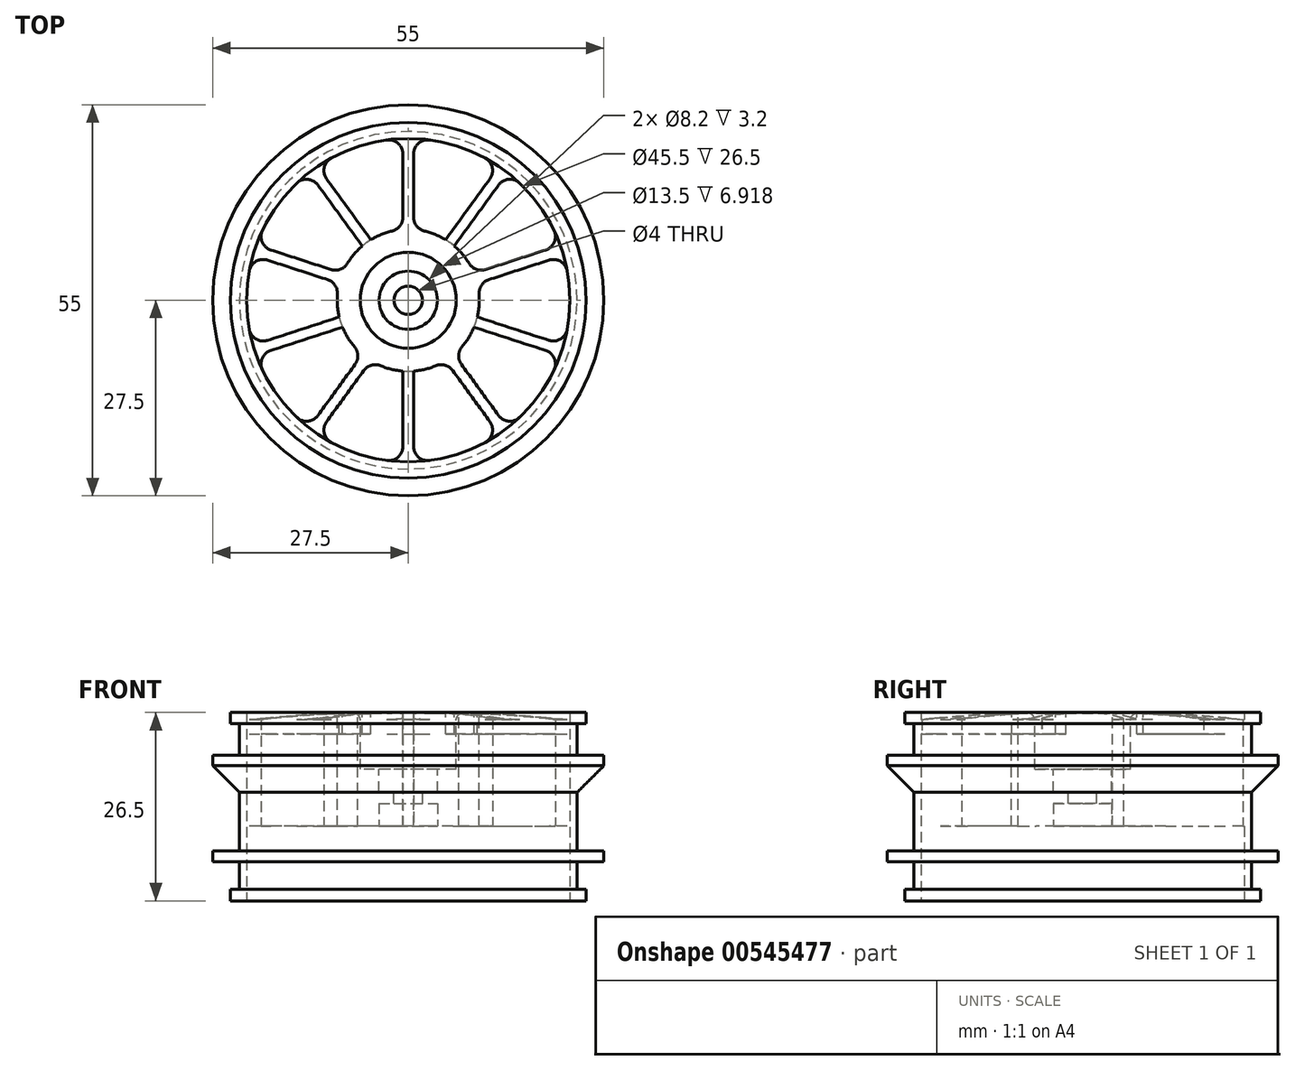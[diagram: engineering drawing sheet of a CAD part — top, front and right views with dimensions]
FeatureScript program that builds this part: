
annotation { "Feature Type Name" : "Feature", "Feature Type Description" : "" }
export const myFeature = defineFeature(function(context is Context, id is Id, definition is map)
    precondition{}
    {
        {
            var Q0;
            Q0=qCreatedBy(makeId("Top.planeOp"),FACE);
            var sketch = newSketch(context, id + "F0", { "sketchPlane" : qUnion([Q0])});
            skCircle(sketch, "E0", {"center": v(0, 0) * mm, "radius": 23.75 * mm});
            skCircle(sketch, "E1", {"center": v(0, 0) * mm, "radius": 22.75 * mm});
            skSolve(sketch);
        }
        {
            var Q0;
            Q0=qSketchRegion(id+"F0",true);
            extrude(context, id + "F1", {"entities" : qUnion([Q0]), "depth" : 26.5 * mm, "offsetDistance" : 25 * mm});
        }
        {
            var Q0;
            Q0=qCreatedBy(makeId("Top.planeOp"),FACE);
            var sketch = newSketch(context, id + "F2", { "sketchPlane" : qUnion([Q0])});
            skCircle(sketch, "E2", {"center": v(0, 0) * mm, "radius": 25 * mm});
            skCircle(sketch, "E3", {"center": v(0, 0) * mm, "radius": 22.75 * mm});
            skSolve(sketch);
        }
        {
            var Q0;
            Q0=qSketchRegion(id+"F2",true);
            extrude(context, id + "F3", {"entities" : qUnion([Q0]), "operationType" : NewBodyOperationType.ADD, "depth" : 1.6 * mm, "offsetDistance" : 25 * mm});
        }
        {
            var Q0;
            Q0=makeQuery(id+"F1.opExtrude","CAP_FACE",FACE,{"disambiguationData":[OSD([sQuery(id+"F0.wireOp",EDGE,"E0"),sQuery(id+"F0.wireOp",EDGE,"E1")])],"isStart":false});
            var sketch = newSketch(context, id + "F4", { "sketchPlane" : qUnion([Q0])});
            skCircle(sketch, "E4", {"center": v(0, 0) * mm, "radius": 22.75 * mm});
            skCircle(sketch, "E5", {"center": v(0, 0) * mm, "radius": 25 * mm});
            skSolve(sketch);
        }
        {
            var Q0;
            Q0=qSketchRegion(id+"F4",true);
            extrude(context, id + "F5", {"entities" : qUnion([Q0]), "operationType" : NewBodyOperationType.ADD, "oppositeDirection" : true, "depth" : 1.6 * mm, "offsetDistance" : 25 * mm});
        }
        {
            var Q0;
            Q0=qCreatedBy(makeId("Top.planeOp"),FACE);
            cPlane(context, id + "F6", {"entities" : qUnion([Q0]), "cplaneType" : CPlaneType.OFFSET, "offset" : 5.5 * mm, "width" : 150 * mm, "height" : 150 * mm});
        }
        {
            var Q0;
            Q0=qCreatedBy(id+"F6.planeOp",FACE);
            var sketch = newSketch(context, id + "F7", { "sketchPlane" : qUnion([Q0])});
            skCircle(sketch, "E6", {"center": v(0, 0) * mm, "radius": 27.5 * mm});
            skCircle(sketch, "E7", {"center": v(0, 0) * mm, "radius": 22.75 * mm});
            skSolve(sketch);
        }
        {
            var Q0;
            Q0=qSketchRegion(id+"F7",true);
            extrude(context, id + "F8", {"entities" : qUnion([Q0]), "operationType" : NewBodyOperationType.ADD, "depth" : 1.5 * mm, "offsetDistance" : 25 * mm});
        }
        {
            var Q0;
            Q0=qCreatedBy(makeId("Top.planeOp"),FACE);
            cPlane(context, id + "F9", {"entities" : qUnion([Q0]), "cplaneType" : CPlaneType.OFFSET, "offset" : 19 * mm, "width" : 150 * mm, "height" : 150 * mm});
        }
        {
            var Q0;
            Q0=qCreatedBy(id+"F9.planeOp",FACE);
            var sketch = newSketch(context, id + "F10", { "sketchPlane" : qUnion([Q0])});
            skCircle(sketch, "E8", {"center": v(0, 0) * mm, "radius": 27.5 * mm});
            skCircle(sketch, "E9", {"center": v(0, 0) * mm, "radius": 22.75 * mm});
            skSolve(sketch);
        }
        {
            var Q0;
            Q0=qSketchRegion(id+"F10",true);
            extrude(context, id + "F11", {"entities" : qUnion([Q0]), "operationType" : NewBodyOperationType.ADD, "depth" : 1.5 * mm, "offsetDistance" : 25 * mm});
        }
        {
            var Q0;
            Q0=makeQuery(id+"F5.boolean.opBoolean","MERGE",FACE,{"derivedFrom":[makeQuery(id+"F1.opExtrude","CAP_FACE",FACE,{"disambiguationData":[OSD([sQuery(id+"F0.wireOp",EDGE,"E0"),sQuery(id+"F0.wireOp",EDGE,"E1")])],"isStart":false}),makeQuery(id+"F5.opExtrude","CAP_FACE",FACE,{"disambiguationData":[OSD([sQuery(id+"F4.wireOp",EDGE,"E4"),sQuery(id+"F4.wireOp",EDGE,"E5")])],"isStart":true})]});
            var sketch = newSketch(context, id + "F12", { "sketchPlane" : qUnion([Q0])});
            skLineSegment(sketch, "E10.top", {"start": v(-0.75, 23) * mm, "end": v(0.75, 23) * mm});
            skLineSegment(sketch, "E10.left", {"start": v(-0.75, 9.97) * mm, "end": v(-0.75, 23) * mm});
            skLineSegment(sketch, "E10.right", {"start": v(0.75, 9.97) * mm, "end": v(0.75, 23) * mm});
            skArc(sketch, "E11", {"start": v(-0.75, 9.97) * mm, "mid": v(-5.88, 8.1) * mm, "end": v(-9.25, 3.8) * mm});
            skLineSegment(sketch, "E12.1.0", {"start": v(9.25, 3.8) * mm, "end": v(21.64, 7.82) * mm});
            skLineSegment(sketch, "E12.1.1", {"start": v(9.72, 2.37) * mm, "end": v(22.1, 6.4) * mm});
            skLineSegment(sketch, "E12.1.2", {"start": v(21.64, 7.82) * mm, "end": v(22.1, 6.4) * mm});
            skLineSegment(sketch, "E12.2.0", {"start": v(6.47, -7.63) * mm, "end": v(14.13, -18.17) * mm});
            skLineSegment(sketch, "E12.2.1", {"start": v(5.25, -8.5) * mm, "end": v(12.91, -19.05) * mm});
            skLineSegment(sketch, "E12.2.2", {"start": v(14.13, -18.17) * mm, "end": v(12.91, -19.05) * mm});
            skLineSegment(sketch, "E12.3.0", {"start": v(-5.25, -8.5) * mm, "end": v(-12.91, -19.05) * mm});
            skLineSegment(sketch, "E12.3.1", {"start": v(-6.47, -7.63) * mm, "end": v(-14.13, -18.17) * mm});
            skLineSegment(sketch, "E12.3.2", {"start": v(-12.91, -19.05) * mm, "end": v(-14.13, -18.17) * mm});
            skLineSegment(sketch, "E12.4.0", {"start": v(-9.72, 2.37) * mm, "end": v(-22.1, 6.4) * mm});
            skLineSegment(sketch, "E12.4.1", {"start": v(-9.25, 3.8) * mm, "end": v(-21.64, 7.82) * mm});
            skLineSegment(sketch, "E12.4.2", {"start": v(-22.1, 6.4) * mm, "end": v(-21.64, 7.82) * mm});
            skLineSegment(sketch, "E12.anchor1", {"start": v(0, 0) * mm, "end": v(-0.75, 9.97) * mm, "construction": true});
            skLineSegment(sketch, "E12.anchor2", {"start": v(0, 0) * mm, "end": v(-9.72, 2.37) * mm, "construction": true});
            skArc(sketch, "E13.trimOffspring", {"start": v(-9.72, 2.37) * mm, "mid": v(-9.51, -3.1) * mm, "end": v(-6.47, -7.63) * mm});
            skArc(sketch, "E14.trimOffspring", {"start": v(-5.25, -8.5) * mm, "mid": v(0, -10) * mm, "end": v(5.25, -8.5) * mm});
            skArc(sketch, "E15.trimOffspring", {"start": v(6.47, -7.63) * mm, "mid": v(9.51, -3.1) * mm, "end": v(9.72, 2.37) * mm});
            skArc(sketch, "E16.trimOffspring", {"start": v(9.25, 3.8) * mm, "mid": v(5.88, 8.1) * mm, "end": v(0.75, 9.97) * mm});
            skSolve(sketch);
        }
        {
            var Q0;
            Q0=qSketchRegion(id+"F12",true);
            extrude(context, id + "F13", {"entities" : qUnion([Q0]), "operationType" : NewBodyOperationType.ADD, "oppositeDirection" : true, "depth" : 16 * mm, "offsetDistance" : 25 * mm});
        }
        {
            var Q0;
            Q0=makeQuery(id+"F11.boolean.opBoolean","INTERSECT",EDGE,{"derivedFrom":[makeQuery(id+"F8.boolean.opBoolean","SPLIT",FACE,{"disambiguationData":[TD([makeQuery(id+"F5.opExtrude","CAP_FACE",FACE,{"disambiguationData":[OSD([sQuery(id+"F4.wireOp",EDGE,"E4"),sQuery(id+"F4.wireOp",EDGE,"E5")])],"isStart":false})])],"derivedFrom":makeQuery(id+"F1.opExtrude","SWEPT_FACE",FACE,{"disambiguationData":[OSD([sQuery(id+"F0.wireOp",EDGE,"E0")])]})}),makeQuery(id+"F11.opExtrude","CAP_FACE",FACE,{"disambiguationData":[OSD([sQuery(id+"F10.wireOp",EDGE,"E8"),sQuery(id+"F10.wireOp",EDGE,"E9")])],"isStart":true})]});
            chamfer(context, id + "F14", {"entities" : qUnion([Q0]), "width" : 3.75 * mm, "tangentPropagation" : true});
        }
        {
            var Q0;
            Q0=makeQuery(id+"F13.boolean.opBoolean","MERGE",FACE,{"derivedFrom":[makeQuery(id+"F5.boolean.opBoolean","MERGE",FACE,{"derivedFrom":[makeQuery(id+"F1.opExtrude","CAP_FACE",FACE,{"disambiguationData":[OSD([sQuery(id+"F0.wireOp",EDGE,"E0"),sQuery(id+"F0.wireOp",EDGE,"E1")])],"isStart":false}),makeQuery(id+"F5.opExtrude","CAP_FACE",FACE,{"disambiguationData":[OSD([sQuery(id+"F4.wireOp",EDGE,"E4"),sQuery(id+"F4.wireOp",EDGE,"E5")])],"isStart":true})]}),makeQuery(id+"F13.opExtrude","CAP_FACE",FACE,{"disambiguationData":[OSD([sQuery(id+"F12.wireOp",EDGE,"E10.top"),sQuery(id+"F12.wireOp",EDGE,"E10.left"),sQuery(id+"F12.wireOp",EDGE,"E10.right"),sQuery(id+"F12.wireOp",EDGE,"E11"),sQuery(id+"F12.wireOp",EDGE,"E12.1.0"),sQuery(id+"F12.wireOp",EDGE,"E12.1.1"),sQuery(id+"F12.wireOp",EDGE,"E12.1.2"),sQuery(id+"F12.wireOp",EDGE,"E12.2.0"),sQuery(id+"F12.wireOp",EDGE,"E12.2.1"),sQuery(id+"F12.wireOp",EDGE,"E12.2.2"),sQuery(id+"F12.wireOp",EDGE,"E12.3.0"),sQuery(id+"F12.wireOp",EDGE,"E12.3.1"),sQuery(id+"F12.wireOp",EDGE,"E12.3.2"),sQuery(id+"F12.wireOp",EDGE,"E12.4.0"),sQuery(id+"F12.wireOp",EDGE,"E12.4.1"),sQuery(id+"F12.wireOp",EDGE,"E12.4.2"),sQuery(id+"F12.wireOp",EDGE,"E13.trimOffspring"),sQuery(id+"F12.wireOp",EDGE,"E14.trimOffspring"),sQuery(id+"F12.wireOp",EDGE,"E15.trimOffspring"),sQuery(id+"F12.wireOp",EDGE,"E16.trimOffspring")])],"isStart":true})]});
            var sketch = newSketch(context, id + "F15", { "sketchPlane" : qUnion([Q0])});
            skArc(sketch, "E17", {"start": v(-0.75, 9.97) * mm, "mid": v(-3.1, 9.51) * mm, "end": v(-5.25, 8.5) * mm});
            skLineSegment(sketch, "E18", {"start": v(-0.75, 9.97) * mm, "end": v(-0.75, 22.97) * mm});
            skLineSegment(sketch, "E19", {"start": v(0.75, 22.97) * mm, "end": v(0.75, 9.97) * mm});
            skLineSegment(sketch, "E20.1.0", {"start": v(-6.47, 7.63) * mm, "end": v(-14.11, 18.14) * mm});
            skLineSegment(sketch, "E20.1.1", {"start": v(-12.9, 19.02) * mm, "end": v(-5.25, 8.5) * mm});
            skLineSegment(sketch, "E20.2.0", {"start": v(-9.72, 2.37) * mm, "end": v(-22.08, 6.38) * mm});
            skLineSegment(sketch, "E20.2.1", {"start": v(-21.62, 7.8) * mm, "end": v(-9.25, 3.8) * mm});
            skLineSegment(sketch, "E20.3.0", {"start": v(-9.25, -3.8) * mm, "end": v(-21.62, -7.81) * mm});
            skLineSegment(sketch, "E20.3.1", {"start": v(-22.08, -6.39) * mm, "end": v(-9.72, -2.37) * mm});
            skLineSegment(sketch, "E20.4.0", {"start": v(-5.25, -8.5) * mm, "end": v(-12.9, -19.03) * mm});
            skLineSegment(sketch, "E20.4.1", {"start": v(-14.1, -18.15) * mm, "end": v(-6.47, -7.63) * mm});
            skLineSegment(sketch, "E20.5.0", {"start": v(0.75, -9.97) * mm, "end": v(0.75, -22.97) * mm});
            skLineSegment(sketch, "E20.5.1", {"start": v(-0.75, -22.97) * mm, "end": v(-0.75, -9.97) * mm});
            skLineSegment(sketch, "E20.6.0", {"start": v(6.47, -7.63) * mm, "end": v(14.11, -18.14) * mm});
            skLineSegment(sketch, "E20.6.1", {"start": v(12.9, -19.02) * mm, "end": v(5.25, -8.5) * mm});
            skLineSegment(sketch, "E20.7.0", {"start": v(9.72, -2.37) * mm, "end": v(22.08, -6.38) * mm});
            skLineSegment(sketch, "E20.7.1", {"start": v(21.62, -7.8) * mm, "end": v(9.25, -3.8) * mm});
            skLineSegment(sketch, "E20.8.0", {"start": v(9.25, 3.8) * mm, "end": v(21.62, 7.81) * mm});
            skLineSegment(sketch, "E20.8.1", {"start": v(22.08, 6.39) * mm, "end": v(9.72, 2.37) * mm});
            skLineSegment(sketch, "E20.9.0", {"start": v(5.25, 8.5) * mm, "end": v(12.9, 19.03) * mm});
            skLineSegment(sketch, "E20.9.1", {"start": v(14.1, 18.15) * mm, "end": v(6.47, 7.63) * mm});
            skArc(sketch, "E21.trimOffspring", {"start": v(-9.72, 2.37) * mm, "mid": v(-10, 0) * mm, "end": v(-9.72, -2.37) * mm});
            skArc(sketch, "E22.trimOffspring", {"start": v(-5.25, -8.5) * mm, "mid": v(-3.1, -9.51) * mm, "end": v(-0.75, -9.97) * mm});
            skArc(sketch, "E23.trimOffspring", {"start": v(9.72, -2.37) * mm, "mid": v(10, 0) * mm, "end": v(9.72, 2.37) * mm});
            skArc(sketch, "E24.trimOffspring", {"start": v(6.47, -7.63) * mm, "mid": v(8.1, -5.88) * mm, "end": v(9.25, -3.8) * mm});
            skArc(sketch, "E25.trimOffspring", {"start": v(0.75, -9.97) * mm, "mid": v(3.1, -9.51) * mm, "end": v(5.25, -8.5) * mm});
            skArc(sketch, "E26.trimOffspring", {"start": v(-9.25, -3.8) * mm, "mid": v(-8.1, -5.88) * mm, "end": v(-6.47, -7.63) * mm});
            skArc(sketch, "E27.trimOffspring", {"start": v(-6.47, 7.63) * mm, "mid": v(-8.1, 5.88) * mm, "end": v(-9.25, 3.8) * mm});
            skArc(sketch, "E28.trimOffspring", {"start": v(5.25, 8.5) * mm, "mid": v(3.1, 9.51) * mm, "end": v(0.75, 9.97) * mm});
            skArc(sketch, "E29.trimOffspring", {"start": v(9.25, 3.8) * mm, "mid": v(8.1, 5.88) * mm, "end": v(6.47, 7.63) * mm});
            skLineSegment(sketch, "E30", {"start": v(-12.9, 19.02) * mm, "end": v(-14.11, 18.14) * mm});
            skLineSegment(sketch, "E31", {"start": v(-21.62, 7.8) * mm, "end": v(-22.08, 6.38) * mm});
            skLineSegment(sketch, "E32", {"start": v(-22.08, -6.39) * mm, "end": v(-21.62, -7.81) * mm});
            skLineSegment(sketch, "E33", {"start": v(-14.1, -18.15) * mm, "end": v(-12.9, -19.03) * mm});
            skLineSegment(sketch, "E34", {"start": v(-0.75, -22.97) * mm, "end": v(0.75, -22.97) * mm});
            skLineSegment(sketch, "E35", {"start": v(14.11, -18.14) * mm, "end": v(12.9, -19.02) * mm});
            skLineSegment(sketch, "E36", {"start": v(22.08, -6.38) * mm, "end": v(21.62, -7.8) * mm});
            skLineSegment(sketch, "E37", {"start": v(21.62, 7.81) * mm, "end": v(22.08, 6.39) * mm});
            skLineSegment(sketch, "E38", {"start": v(12.9, 19.03) * mm, "end": v(14.1, 18.15) * mm});
            skLineSegment(sketch, "E39", {"start": v(-0.75, 22.97) * mm, "end": v(0.75, 22.97) * mm});
            skSolve(sketch);
        }
        {
            var Q0;
            Q0=qSketchRegion(id+"F15",true);
            extrude(context, id + "F16", {"entities" : qUnion([Q0]), "operationType" : NewBodyOperationType.ADD, "oppositeDirection" : true, "depth" : 3 * mm, "offsetDistance" : 25 * mm});
        }
        {
            var Q0;
            Q0=makeQuery(id+"F16.boolean.opBoolean","INTERSECT",EDGE,{"derivedFrom":[makeQuery(id+"F1.opExtrude","SWEPT_FACE",FACE,{"disambiguationData":[OSD([sQuery(id+"F0.wireOp",EDGE,"E1")])]}),makeQuery(id+"F16.opExtrude","SWEPT_FACE",FACE,{"disambiguationData":[OSD([sQuery(id+"F15.wireOp",EDGE,"E20.1.0")])]})]});
            var Q1;
            Q1=makeQuery(id+"F16.boolean.opBoolean","INTERSECT",EDGE,{"derivedFrom":[makeQuery(id+"F1.opExtrude","SWEPT_FACE",FACE,{"disambiguationData":[OSD([sQuery(id+"F0.wireOp",EDGE,"E1")])]}),makeQuery(id+"F16.opExtrude","SWEPT_FACE",FACE,{"disambiguationData":[OSD([sQuery(id+"F15.wireOp",EDGE,"E20.1.1")])]})]});
            var Q2;
            Q2=makeQuery(id+"F16.opExtrude","SWEPT_EDGE",EDGE,{"disambiguationData":[OSD([sQuery(id+"F12.wireOp",EDGE,"E11"),sQuery(id+"F15.wireOp",EDGE,"E20.1.0"),sQuery(id+"F15.wireOp",EDGE,"E27.trimOffspring")])]});
            var Q3;
            Q3=makeQuery(id+"F13.boolean.opBoolean","INTERSECT",EDGE,{"derivedFrom":[makeQuery(id+"F1.opExtrude","SWEPT_FACE",FACE,{"disambiguationData":[OSD([sQuery(id+"F0.wireOp",EDGE,"E1")])]}),makeQuery(id+"F13.opExtrude","SWEPT_FACE",FACE,{"disambiguationData":[OSD([sQuery(id+"F12.wireOp",EDGE,"E12.4.1")])]})]});
            var Q4;
            Q4=makeQuery(id+"F13.opExtrude","SWEPT_EDGE",EDGE,{"disambiguationData":[OSD([sQuery(id+"F12.wireOp",EDGE,"E11"),sQuery(id+"F12.wireOp",EDGE,"E12.4.1")])]});
            var Q5;
            Q5=makeQuery(id+"F13.opExtrude","SWEPT_EDGE",EDGE,{"disambiguationData":[OSD([sQuery(id+"F12.wireOp",EDGE,"E10.left"),sQuery(id+"F12.wireOp",EDGE,"E11")])]});
            var Q6;
            Q6=makeQuery(id+"F13.boolean.opBoolean","INTERSECT",EDGE,{"derivedFrom":[makeQuery(id+"F1.opExtrude","SWEPT_FACE",FACE,{"disambiguationData":[OSD([sQuery(id+"F0.wireOp",EDGE,"E1")])]}),makeQuery(id+"F13.opExtrude","SWEPT_FACE",FACE,{"disambiguationData":[OSD([sQuery(id+"F12.wireOp",EDGE,"E10.left")])]})]});
            var Q7;
            Q7=makeQuery(id+"F16.opExtrude","SWEPT_EDGE",EDGE,{"disambiguationData":[OSD([sQuery(id+"F12.wireOp",EDGE,"E11"),sQuery(id+"F15.wireOp",EDGE,"E17"),sQuery(id+"F15.wireOp",EDGE,"E20.1.1")])]});
            var Q8;
            Q8=makeQuery(id+"F16.opExtrude","SWEPT_EDGE",EDGE,{"disambiguationData":[OSD([sQuery(id+"F12.wireOp",EDGE,"E16.trimOffspring"),sQuery(id+"F15.wireOp",EDGE,"E20.9.0"),sQuery(id+"F15.wireOp",EDGE,"E28.trimOffspring")])]});
            var Q9;
            Q9=makeQuery(id+"F13.opExtrude","SWEPT_EDGE",EDGE,{"disambiguationData":[OSD([sQuery(id+"F12.wireOp",EDGE,"E10.right"),sQuery(id+"F12.wireOp",EDGE,"E16.trimOffspring")])]});
            var Q10;
            Q10=makeQuery(id+"F13.opExtrude","SWEPT_EDGE",EDGE,{"disambiguationData":[OSD([sQuery(id+"F12.wireOp",EDGE,"E12.1.0"),sQuery(id+"F12.wireOp",EDGE,"E16.trimOffspring")])]});
            var Q11;
            Q11=makeQuery(id+"F13.boolean.opBoolean","INTERSECT",EDGE,{"derivedFrom":[makeQuery(id+"F1.opExtrude","SWEPT_FACE",FACE,{"disambiguationData":[OSD([sQuery(id+"F0.wireOp",EDGE,"E1")])]}),makeQuery(id+"F13.opExtrude","SWEPT_FACE",FACE,{"disambiguationData":[OSD([sQuery(id+"F12.wireOp",EDGE,"E10.right")])]})]});
            var Q12;
            Q12=makeQuery(id+"F16.boolean.opBoolean","INTERSECT",EDGE,{"derivedFrom":[makeQuery(id+"F1.opExtrude","SWEPT_FACE",FACE,{"disambiguationData":[OSD([sQuery(id+"F0.wireOp",EDGE,"E1")])]}),makeQuery(id+"F16.opExtrude","SWEPT_FACE",FACE,{"disambiguationData":[OSD([sQuery(id+"F15.wireOp",EDGE,"E20.9.0")])]})]});
            var Q13;
            Q13=makeQuery(id+"F13.boolean.opBoolean","INTERSECT",EDGE,{"derivedFrom":[makeQuery(id+"F1.opExtrude","SWEPT_FACE",FACE,{"disambiguationData":[OSD([sQuery(id+"F0.wireOp",EDGE,"E1")])]}),makeQuery(id+"F13.opExtrude","SWEPT_FACE",FACE,{"disambiguationData":[OSD([sQuery(id+"F12.wireOp",EDGE,"E12.1.0")])]})]});
            var Q14;
            Q14=makeQuery(id+"F13.boolean.opBoolean","INTERSECT",EDGE,{"derivedFrom":[makeQuery(id+"F1.opExtrude","SWEPT_FACE",FACE,{"disambiguationData":[OSD([sQuery(id+"F0.wireOp",EDGE,"E1")])]}),makeQuery(id+"F13.opExtrude","SWEPT_FACE",FACE,{"disambiguationData":[OSD([sQuery(id+"F12.wireOp",EDGE,"E12.1.1")])]})]});
            var Q15;
            Q15=makeQuery(id+"F13.opExtrude","SWEPT_EDGE",EDGE,{"disambiguationData":[OSD([sQuery(id+"F12.wireOp",EDGE,"E12.1.1"),sQuery(id+"F12.wireOp",EDGE,"E15.trimOffspring")])]});
            var Q16;
            Q16=makeQuery(id+"F16.opExtrude","SWEPT_EDGE",EDGE,{"disambiguationData":[OSD([sQuery(id+"F12.wireOp",EDGE,"E15.trimOffspring"),sQuery(id+"F15.wireOp",EDGE,"E20.7.1"),sQuery(id+"F15.wireOp",EDGE,"E24.trimOffspring")])]});
            var Q17;
            Q17=makeQuery(id+"F13.opExtrude","SWEPT_EDGE",EDGE,{"disambiguationData":[OSD([sQuery(id+"F12.wireOp",EDGE,"E12.2.0"),sQuery(id+"F12.wireOp",EDGE,"E15.trimOffspring")])]});
            var Q18;
            Q18=makeQuery(id+"F16.opExtrude","SWEPT_EDGE",EDGE,{"disambiguationData":[OSD([sQuery(id+"F12.wireOp",EDGE,"E14.trimOffspring"),sQuery(id+"F15.wireOp",EDGE,"E20.5.0"),sQuery(id+"F15.wireOp",EDGE,"E25.trimOffspring")])]});
            var Q19;
            Q19=makeQuery(id+"F13.boolean.opBoolean","INTERSECT",EDGE,{"derivedFrom":[makeQuery(id+"F1.opExtrude","SWEPT_FACE",FACE,{"disambiguationData":[OSD([sQuery(id+"F0.wireOp",EDGE,"E1")])]}),makeQuery(id+"F13.opExtrude","SWEPT_FACE",FACE,{"disambiguationData":[OSD([sQuery(id+"F12.wireOp",EDGE,"E12.3.0")])]})]});
            var Q20;
            Q20=makeQuery(id+"F16.boolean.opBoolean","INTERSECT",EDGE,{"derivedFrom":[makeQuery(id+"F1.opExtrude","SWEPT_FACE",FACE,{"disambiguationData":[OSD([sQuery(id+"F0.wireOp",EDGE,"E1")])]}),makeQuery(id+"F16.opExtrude","SWEPT_FACE",FACE,{"disambiguationData":[OSD([sQuery(id+"F15.wireOp",EDGE,"E20.3.0")])]})]});
            var Q21;
            Q21=makeQuery(id+"F13.boolean.opBoolean","INTERSECT",EDGE,{"derivedFrom":[makeQuery(id+"F1.opExtrude","SWEPT_FACE",FACE,{"disambiguationData":[OSD([sQuery(id+"F0.wireOp",EDGE,"E1")])]}),makeQuery(id+"F13.opExtrude","SWEPT_FACE",FACE,{"disambiguationData":[OSD([sQuery(id+"F12.wireOp",EDGE,"E12.4.0")])]})]});
            var Q22;
            Q22=makeQuery(id+"F16.boolean.opBoolean","INTERSECT",EDGE,{"derivedFrom":[makeQuery(id+"F1.opExtrude","SWEPT_FACE",FACE,{"disambiguationData":[OSD([sQuery(id+"F0.wireOp",EDGE,"E1")])]}),makeQuery(id+"F16.opExtrude","SWEPT_FACE",FACE,{"disambiguationData":[OSD([sQuery(id+"F15.wireOp",EDGE,"E20.9.1")])]})]});
            var Q23;
            Q23=makeQuery(id+"F16.boolean.opBoolean","INTERSECT",EDGE,{"derivedFrom":[makeQuery(id+"F1.opExtrude","SWEPT_FACE",FACE,{"disambiguationData":[OSD([sQuery(id+"F0.wireOp",EDGE,"E1")])]}),makeQuery(id+"F16.opExtrude","SWEPT_FACE",FACE,{"disambiguationData":[OSD([sQuery(id+"F15.wireOp",EDGE,"E20.7.1")])]})]});
            var Q24;
            Q24=makeQuery(id+"F16.opExtrude","SWEPT_EDGE",EDGE,{"disambiguationData":[OSD([sQuery(id+"F12.wireOp",EDGE,"E13.trimOffspring"),sQuery(id+"F15.wireOp",EDGE,"E20.3.0"),sQuery(id+"F15.wireOp",EDGE,"E26.trimOffspring")])]});
            var Q25;
            Q25=makeQuery(id+"F13.opExtrude","SWEPT_EDGE",EDGE,{"disambiguationData":[OSD([sQuery(id+"F12.wireOp",EDGE,"E12.4.0"),sQuery(id+"F12.wireOp",EDGE,"E13.trimOffspring")])]});
            var Q26;
            Q26=makeQuery(id+"F13.opExtrude","SWEPT_EDGE",EDGE,{"disambiguationData":[OSD([sQuery(id+"F12.wireOp",EDGE,"E12.3.1"),sQuery(id+"F12.wireOp",EDGE,"E13.trimOffspring")])]});
            var Q27;
            Q27=makeQuery(id+"F16.opExtrude","SWEPT_EDGE",EDGE,{"disambiguationData":[OSD([sQuery(id+"F12.wireOp",EDGE,"E14.trimOffspring"),sQuery(id+"F15.wireOp",EDGE,"E20.5.1"),sQuery(id+"F15.wireOp",EDGE,"E22.trimOffspring")])]});
            var Q28;
            Q28=makeQuery(id+"F13.opExtrude","SWEPT_EDGE",EDGE,{"disambiguationData":[OSD([sQuery(id+"F12.wireOp",EDGE,"E12.2.1"),sQuery(id+"F12.wireOp",EDGE,"E14.trimOffspring")])]});
            var Q29;
            Q29=makeQuery(id+"F13.boolean.opBoolean","INTERSECT",EDGE,{"derivedFrom":[makeQuery(id+"F1.opExtrude","SWEPT_FACE",FACE,{"disambiguationData":[OSD([sQuery(id+"F0.wireOp",EDGE,"E1")])]}),makeQuery(id+"F13.opExtrude","SWEPT_FACE",FACE,{"disambiguationData":[OSD([sQuery(id+"F12.wireOp",EDGE,"E12.2.1")])]})]});
            var Q30;
            Q30=makeQuery(id+"F13.boolean.opBoolean","INTERSECT",EDGE,{"derivedFrom":[makeQuery(id+"F1.opExtrude","SWEPT_FACE",FACE,{"disambiguationData":[OSD([sQuery(id+"F0.wireOp",EDGE,"E1")])]}),makeQuery(id+"F13.opExtrude","SWEPT_FACE",FACE,{"disambiguationData":[OSD([sQuery(id+"F12.wireOp",EDGE,"E12.2.0")])]})]});
            var Q31;
            Q31=makeQuery(id+"F16.boolean.opBoolean","INTERSECT",EDGE,{"derivedFrom":[makeQuery(id+"F1.opExtrude","SWEPT_FACE",FACE,{"disambiguationData":[OSD([sQuery(id+"F0.wireOp",EDGE,"E1")])]}),makeQuery(id+"F16.opExtrude","SWEPT_FACE",FACE,{"disambiguationData":[OSD([sQuery(id+"F15.wireOp",EDGE,"E20.5.0")])]})]});
            var Q32;
            Q32=makeQuery(id+"F16.boolean.opBoolean","INTERSECT",EDGE,{"derivedFrom":[makeQuery(id+"F1.opExtrude","SWEPT_FACE",FACE,{"disambiguationData":[OSD([sQuery(id+"F0.wireOp",EDGE,"E1")])]}),makeQuery(id+"F16.opExtrude","SWEPT_FACE",FACE,{"disambiguationData":[OSD([sQuery(id+"F15.wireOp",EDGE,"E20.5.1")])]})]});
            var Q33;
            Q33=makeQuery(id+"F13.boolean.opBoolean","INTERSECT",EDGE,{"derivedFrom":[makeQuery(id+"F1.opExtrude","SWEPT_FACE",FACE,{"disambiguationData":[OSD([sQuery(id+"F0.wireOp",EDGE,"E1")])]}),makeQuery(id+"F13.opExtrude","SWEPT_FACE",FACE,{"disambiguationData":[OSD([sQuery(id+"F12.wireOp",EDGE,"E12.3.1")])]})]});
            var Q34;
            Q34=makeQuery(id+"F16.boolean.opBoolean","INTERSECT",EDGE,{"derivedFrom":[makeQuery(id+"F1.opExtrude","SWEPT_FACE",FACE,{"disambiguationData":[OSD([sQuery(id+"F0.wireOp",EDGE,"E1")])]}),makeQuery(id+"F16.opExtrude","SWEPT_FACE",FACE,{"disambiguationData":[OSD([sQuery(id+"F15.wireOp",EDGE,"E20.3.1")])]})]});
            var Q35;
            Q35=makeQuery(id+"F13.opExtrude","SWEPT_EDGE",EDGE,{"disambiguationData":[OSD([sQuery(id+"F12.wireOp",EDGE,"E12.3.0"),sQuery(id+"F12.wireOp",EDGE,"E14.trimOffspring")])]});
            var Q36;
            Q36=makeQuery(id+"F16.opExtrude","SWEPT_EDGE",EDGE,{"disambiguationData":[OSD([sQuery(id+"F12.wireOp",EDGE,"E16.trimOffspring"),sQuery(id+"F15.wireOp",EDGE,"E20.9.1"),sQuery(id+"F15.wireOp",EDGE,"E29.trimOffspring")])]});
            var Q37;
            Q37=makeQuery(id+"F16.opExtrude","SWEPT_EDGE",EDGE,{"disambiguationData":[OSD([sQuery(id+"F12.wireOp",EDGE,"E15.trimOffspring"),sQuery(id+"F15.wireOp",EDGE,"E20.7.0"),sQuery(id+"F15.wireOp",EDGE,"E23.trimOffspring")])]});
            var Q38;
            Q38=makeQuery(id+"F16.boolean.opBoolean","INTERSECT",EDGE,{"derivedFrom":[makeQuery(id+"F1.opExtrude","SWEPT_FACE",FACE,{"disambiguationData":[OSD([sQuery(id+"F0.wireOp",EDGE,"E1")])]}),makeQuery(id+"F16.opExtrude","SWEPT_FACE",FACE,{"disambiguationData":[OSD([sQuery(id+"F15.wireOp",EDGE,"E20.7.0")])]})]});
            var Q39;
            Q39=makeQuery(id+"F16.opExtrude","SWEPT_EDGE",EDGE,{"disambiguationData":[OSD([sQuery(id+"F12.wireOp",EDGE,"E13.trimOffspring"),sQuery(id+"F15.wireOp",EDGE,"E20.3.1"),sQuery(id+"F15.wireOp",EDGE,"E21.trimOffspring")])]});
            fillet(context, id + "F17", {"entities" : qUnion([Q0, Q1, Q2, Q3, Q4, Q5, Q6, Q7, Q8, Q9, Q10, Q11, Q12, Q13, Q14, Q15, Q16, Q17, Q18, Q19, Q20, Q21, Q22, Q23, Q24, Q25, Q26, Q27, Q28, Q29, Q30, Q31, Q32, Q33, Q34, Q35, Q36, Q37, Q38, Q39]), "radius" : 2 * mm, "tangentPropagation" : true, "allowEdgeOverflow" : false});
        }
        {
            var Q0;
            Q0=qCreatedBy(makeId("Front.planeOp"),FACE);
            var sketch = newSketch(context, id + "F18", { "sketchPlane" : qUnion([Q0])});
            skLineSegment(sketch, "E40", {"start": v(0, 27.5) * mm, "end": v(22.75, 27.5) * mm});
            skLineSegment(sketch, "E41", {"start": v(22.75, 27.5) * mm, "end": v(22.75, 25.5) * mm});
            skFitSpline(sketch, "E42", {"points": [v(22.75, 25.5) * mm, v(12.74, 26.28) * mm, v(0, 26.5) * mm], "startDerivative": vector(-15.68, 1.36) * mm, "endDerivative": vector(-21.9, 0.46) * mm});
            skLineSegment(sketch, "E43", {"start": v(0, 26.5) * mm, "end": v(0, 27.5) * mm});
            skSolve(sketch);
        }
        {
            var Q0;
            Q0=qSketchRegion(id+"F18",true);
            var Q1;
            Q1=sQuery(id+"F18.wireOp",EDGE,"E43");
            revolve(context, id + "F19", {"operationType" : NewBodyOperationType.REMOVE, "entities" : qUnion([Q0]), "axis" : qUnion([Q1]), "revolveType" : RevolveType.FULL});
        }
        {
            var Q0;
            Q0=makeQuery(id+"F16.boolean.opBoolean","MERGE",FACE,{"derivedFrom":[makeQuery(id+"F13.boolean.opBoolean","MERGE",FACE,{"derivedFrom":[makeQuery(id+"F5.boolean.opBoolean","MERGE",FACE,{"derivedFrom":[makeQuery(id+"F1.opExtrude","CAP_FACE",FACE,{"disambiguationData":[OSD([sQuery(id+"F0.wireOp",EDGE,"E0"),sQuery(id+"F0.wireOp",EDGE,"E1")])],"isStart":false}),makeQuery(id+"F5.opExtrude","CAP_FACE",FACE,{"disambiguationData":[OSD([sQuery(id+"F4.wireOp",EDGE,"E4"),sQuery(id+"F4.wireOp",EDGE,"E5")])],"isStart":true})]}),makeQuery(id+"F13.opExtrude","CAP_FACE",FACE,{"disambiguationData":[OSD([sQuery(id+"F12.wireOp",EDGE,"E10.top"),sQuery(id+"F12.wireOp",EDGE,"E10.left"),sQuery(id+"F12.wireOp",EDGE,"E10.right"),sQuery(id+"F12.wireOp",EDGE,"E11"),sQuery(id+"F12.wireOp",EDGE,"E12.1.0"),sQuery(id+"F12.wireOp",EDGE,"E12.1.1"),sQuery(id+"F12.wireOp",EDGE,"E12.1.2"),sQuery(id+"F12.wireOp",EDGE,"E12.2.0"),sQuery(id+"F12.wireOp",EDGE,"E12.2.1"),sQuery(id+"F12.wireOp",EDGE,"E12.2.2"),sQuery(id+"F12.wireOp",EDGE,"E12.3.0"),sQuery(id+"F12.wireOp",EDGE,"E12.3.1"),sQuery(id+"F12.wireOp",EDGE,"E12.3.2"),sQuery(id+"F12.wireOp",EDGE,"E12.4.0"),sQuery(id+"F12.wireOp",EDGE,"E12.4.1"),sQuery(id+"F12.wireOp",EDGE,"E12.4.2"),sQuery(id+"F12.wireOp",EDGE,"E13.trimOffspring"),sQuery(id+"F12.wireOp",EDGE,"E14.trimOffspring"),sQuery(id+"F12.wireOp",EDGE,"E15.trimOffspring"),sQuery(id+"F12.wireOp",EDGE,"E16.trimOffspring")])],"isStart":true})]}),makeQuery(id+"F16.opExtrude","CAP_FACE",FACE,{"disambiguationData":[OSD([sQuery(id+"F15.wireOp",EDGE,"E17"),sQuery(id+"F15.wireOp",EDGE,"E18"),sQuery(id+"F15.wireOp",EDGE,"E19"),sQuery(id+"F15.wireOp",EDGE,"E20.1.0"),sQuery(id+"F15.wireOp",EDGE,"E20.1.1"),sQuery(id+"F15.wireOp",EDGE,"E20.2.0"),sQuery(id+"F15.wireOp",EDGE,"E20.2.1"),sQuery(id+"F15.wireOp",EDGE,"E20.3.0"),sQuery(id+"F15.wireOp",EDGE,"E20.3.1"),sQuery(id+"F15.wireOp",EDGE,"E20.4.0"),sQuery(id+"F15.wireOp",EDGE,"E20.4.1"),sQuery(id+"F15.wireOp",EDGE,"E20.5.0"),sQuery(id+"F15.wireOp",EDGE,"E20.5.1"),sQuery(id+"F15.wireOp",EDGE,"E20.6.0"),sQuery(id+"F15.wireOp",EDGE,"E20.6.1"),sQuery(id+"F15.wireOp",EDGE,"E20.7.0"),sQuery(id+"F15.wireOp",EDGE,"E20.7.1"),sQuery(id+"F15.wireOp",EDGE,"E20.8.0"),sQuery(id+"F15.wireOp",EDGE,"E20.8.1"),sQuery(id+"F15.wireOp",EDGE,"E20.9.0"),sQuery(id+"F15.wireOp",EDGE,"E20.9.1"),sQuery(id+"F15.wireOp",EDGE,"E21.trimOffspring"),sQuery(id+"F15.wireOp",EDGE,"E22.trimOffspring"),sQuery(id+"F15.wireOp",EDGE,"E23.trimOffspring"),sQuery(id+"F15.wireOp",EDGE,"E24.trimOffspring"),sQuery(id+"F15.wireOp",EDGE,"E25.trimOffspring"),sQuery(id+"F15.wireOp",EDGE,"E26.trimOffspring"),sQuery(id+"F15.wireOp",EDGE,"E27.trimOffspring"),sQuery(id+"F15.wireOp",EDGE,"E28.trimOffspring"),sQuery(id+"F15.wireOp",EDGE,"E29.trimOffspring"),sQuery(id+"F15.wireOp",EDGE,"E30"),sQuery(id+"F15.wireOp",EDGE,"E31"),sQuery(id+"F15.wireOp",EDGE,"E32"),sQuery(id+"F15.wireOp",EDGE,"E33"),sQuery(id+"F15.wireOp",EDGE,"E34"),sQuery(id+"F15.wireOp",EDGE,"E35"),sQuery(id+"F15.wireOp",EDGE,"E36"),sQuery(id+"F15.wireOp",EDGE,"E37"),sQuery(id+"F15.wireOp",EDGE,"E38"),sQuery(id+"F15.wireOp",EDGE,"E39")])],"isStart":true})]});
            var sketch = newSketch(context, id + "F20", { "sketchPlane" : qUnion([Q0])});
            skCircle(sketch, "E44", {"center": v(0, 0) * mm, "radius": 6.75 * mm});
            skSolve(sketch);
        }
        {
            var Q0;
            Q0=qSketchRegion(id+"F20",true);
            extrude(context, id + "F21", {"entities" : qUnion([Q0]), "operationType" : NewBodyOperationType.REMOVE, "oppositeDirection" : true, "depth" : 8 * mm, "offsetDistance" : 25 * mm});
        }
        {
            var Q0;
            Q0=makeQuery(id+"F21.boolean.opBoolean","INTERSECT",EDGE,{"derivedFrom":[makeQuery(id+"F19.boolean.opBoolean","COPY",FACE,{"derivedFrom":makeQuery(id+"F19.opRevolve","SWEPT_FACE",FACE,{"disambiguationData":[OSD([sQuery(id+"F18.wireOp",EDGE,"E42")])]})}),makeQuery(id+"F21.opExtrude","SWEPT_FACE",FACE,{"disambiguationData":[OSD([sQuery(id+"F20.wireOp",EDGE,"E44")])]})]});
            fillet(context, id + "F22", {"entities" : qUnion([Q0]), "radius" : 1 * mm, "tangentPropagation" : true, "allowEdgeOverflow" : false});
        }
        {
            var Q0;
            Q0=makeQuery(id+"F21.boolean.opBoolean","COPY",FACE,{"derivedFrom":makeQuery(id+"F21.opExtrude","CAP_FACE",FACE,{"disambiguationData":[OSD([sQuery(id+"F20.wireOp",EDGE,"E44")])],"isStart":false})});
            var sketch = newSketch(context, id + "F23", { "sketchPlane" : qUnion([Q0])});
            skCircle(sketch, "E45", {"center": v(0, 0) * mm, "radius": 4.1 * mm});
            skSolve(sketch);
        }
        {
            var Q0;
            Q0=qSketchRegion(id+"F23",true);
            extrude(context, id + "F24", {"entities" : qUnion([Q0]), "operationType" : NewBodyOperationType.REMOVE, "oppositeDirection" : true, "depth" : 3.2 * mm, "offsetDistance" : 25 * mm});
        }
        {
            var Q0;
            Q0=makeQuery(id+"F13.opExtrude","CAP_FACE",FACE,{"disambiguationData":[OSD([sQuery(id+"F12.wireOp",EDGE,"E10.top"),sQuery(id+"F12.wireOp",EDGE,"E10.left"),sQuery(id+"F12.wireOp",EDGE,"E10.right"),sQuery(id+"F12.wireOp",EDGE,"E11"),sQuery(id+"F12.wireOp",EDGE,"E12.1.0"),sQuery(id+"F12.wireOp",EDGE,"E12.1.1"),sQuery(id+"F12.wireOp",EDGE,"E12.1.2"),sQuery(id+"F12.wireOp",EDGE,"E12.2.0"),sQuery(id+"F12.wireOp",EDGE,"E12.2.1"),sQuery(id+"F12.wireOp",EDGE,"E12.2.2"),sQuery(id+"F12.wireOp",EDGE,"E12.3.0"),sQuery(id+"F12.wireOp",EDGE,"E12.3.1"),sQuery(id+"F12.wireOp",EDGE,"E12.3.2"),sQuery(id+"F12.wireOp",EDGE,"E12.4.0"),sQuery(id+"F12.wireOp",EDGE,"E12.4.1"),sQuery(id+"F12.wireOp",EDGE,"E12.4.2"),sQuery(id+"F12.wireOp",EDGE,"E13.trimOffspring"),sQuery(id+"F12.wireOp",EDGE,"E14.trimOffspring"),sQuery(id+"F12.wireOp",EDGE,"E15.trimOffspring"),sQuery(id+"F12.wireOp",EDGE,"E16.trimOffspring")])],"isStart":false});
            var sketch = newSketch(context, id + "F25", { "sketchPlane" : qUnion([Q0])});
            skCircle(sketch, "E46", {"center": v(0, 0) * mm, "radius": 4.1 * mm});
            skSolve(sketch);
        }
        {
            var Q0;
            Q0=qSketchRegion(id+"F25",true);
            extrude(context, id + "F26", {"entities" : qUnion([Q0]), "operationType" : NewBodyOperationType.REMOVE, "oppositeDirection" : true, "depth" : 3.2 * mm, "offsetDistance" : 25 * mm});
        }
        {
            var Q0;
            Q0=makeQuery(id+"F24.boolean.opBoolean","COPY",FACE,{"derivedFrom":makeQuery(id+"F24.opExtrude","CAP_FACE",FACE,{"disambiguationData":[OSD([sQuery(id+"F23.wireOp",EDGE,"E45")])],"isStart":false})});
            var sketch = newSketch(context, id + "F27", { "sketchPlane" : qUnion([Q0])});
            skCircle(sketch, "E47", {"center": v(0, 0) * mm, "radius": 2 * mm});
            skSolve(sketch);
        }
        {
            var Q0;
            Q0=qSketchRegion(id+"F27",true);
            extrude(context, id + "F28", {"entities" : qUnion([Q0]), "operationType" : NewBodyOperationType.REMOVE, "oppositeDirection" : true, "depth" : 25 * mm, "offsetDistance" : 25 * mm});
        }
    });
